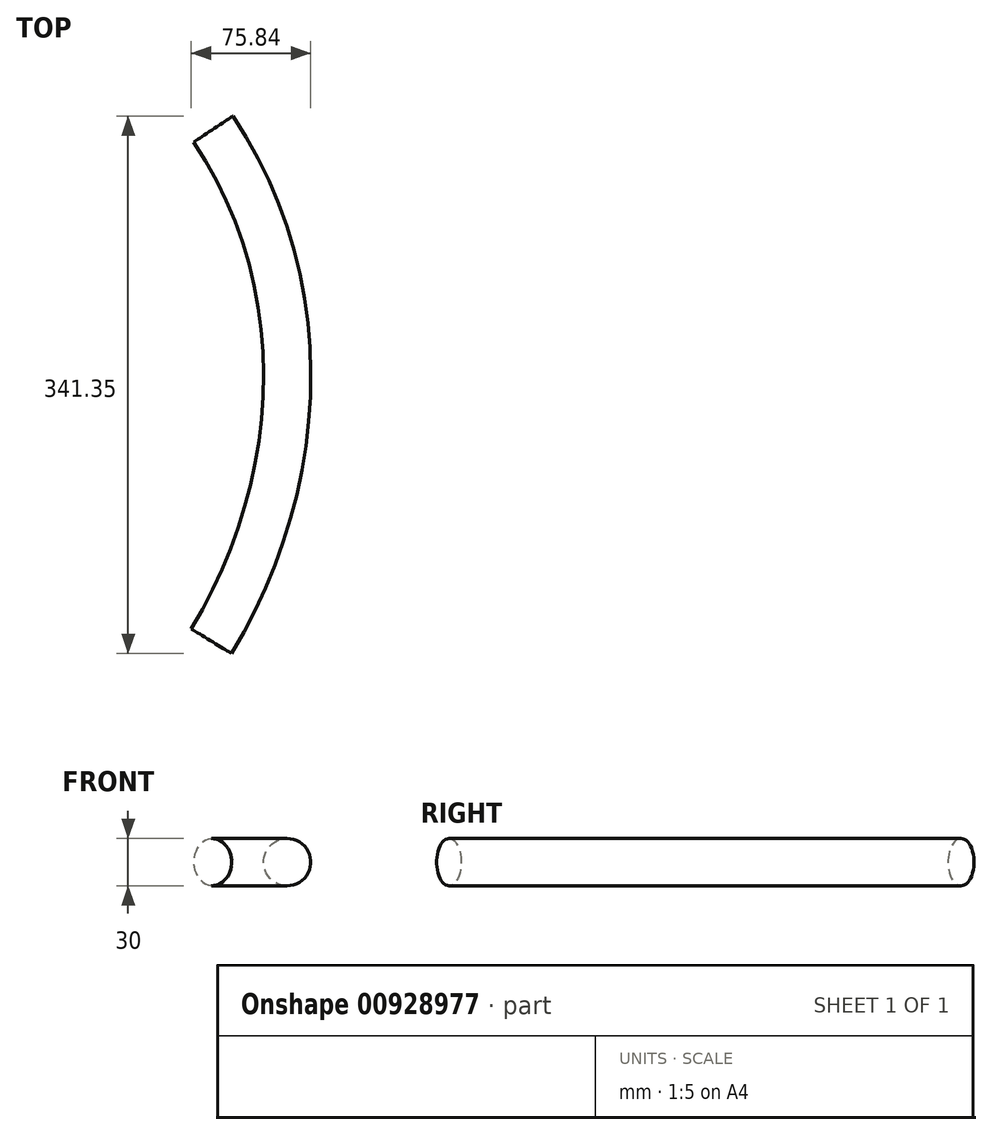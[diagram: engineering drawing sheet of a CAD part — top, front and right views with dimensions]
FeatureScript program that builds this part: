
annotation { "Feature Type Name" : "Feature", "Feature Type Description" : "" }
export const myFeature = defineFeature(function(context is Context, id is Id, definition is map)
    precondition{}
    {
        {
            var Q0;
            Q0=qCreatedBy(makeId("Front.planeOp"),FACE);
            var sketch = newSketch(context, id + "F0", { "sketchPlane" : qUnion([Q0])});
            skCircle(sketch, "E0", {"center": v(0, 0) * mm, "radius": 15 * mm});
            skSolve(sketch);
        }
        {
            var Q0;
            Q0=qCreatedBy(makeId("Top.planeOp"),FACE);
            var sketch = newSketch(context, id + "F1", { "sketchPlane" : qUnion([Q0])});
            skFitSpline(sketch, "E1", {"points": [v(0, 185.63) * mm, v(0, -200) * mm], "startDerivative": vector(225.02, -334.66) * mm, "endDerivative": vector(-225.02, -374.23) * mm});
            skSolve(sketch);
        }
        {
            var Q0;
            Q0=makeQuery(id+"F0.imprint","IMPRINT",FACE,{"disambiguationData":[TD([[makeQuery(id+"F0.imprint","IMPRINT",EDGE,{"derivedFrom":sQuery(id+"F0.wireOp",EDGE,"E0")}),1.0]])]});
            var Q1;
            Q1=sQuery(id+"F1.wireOp",EDGE,"E1");
            sweep(context, id + "F2", {"profiles" : qUnion([Q0]), "path" : qUnion([Q1])});
        }
    });
